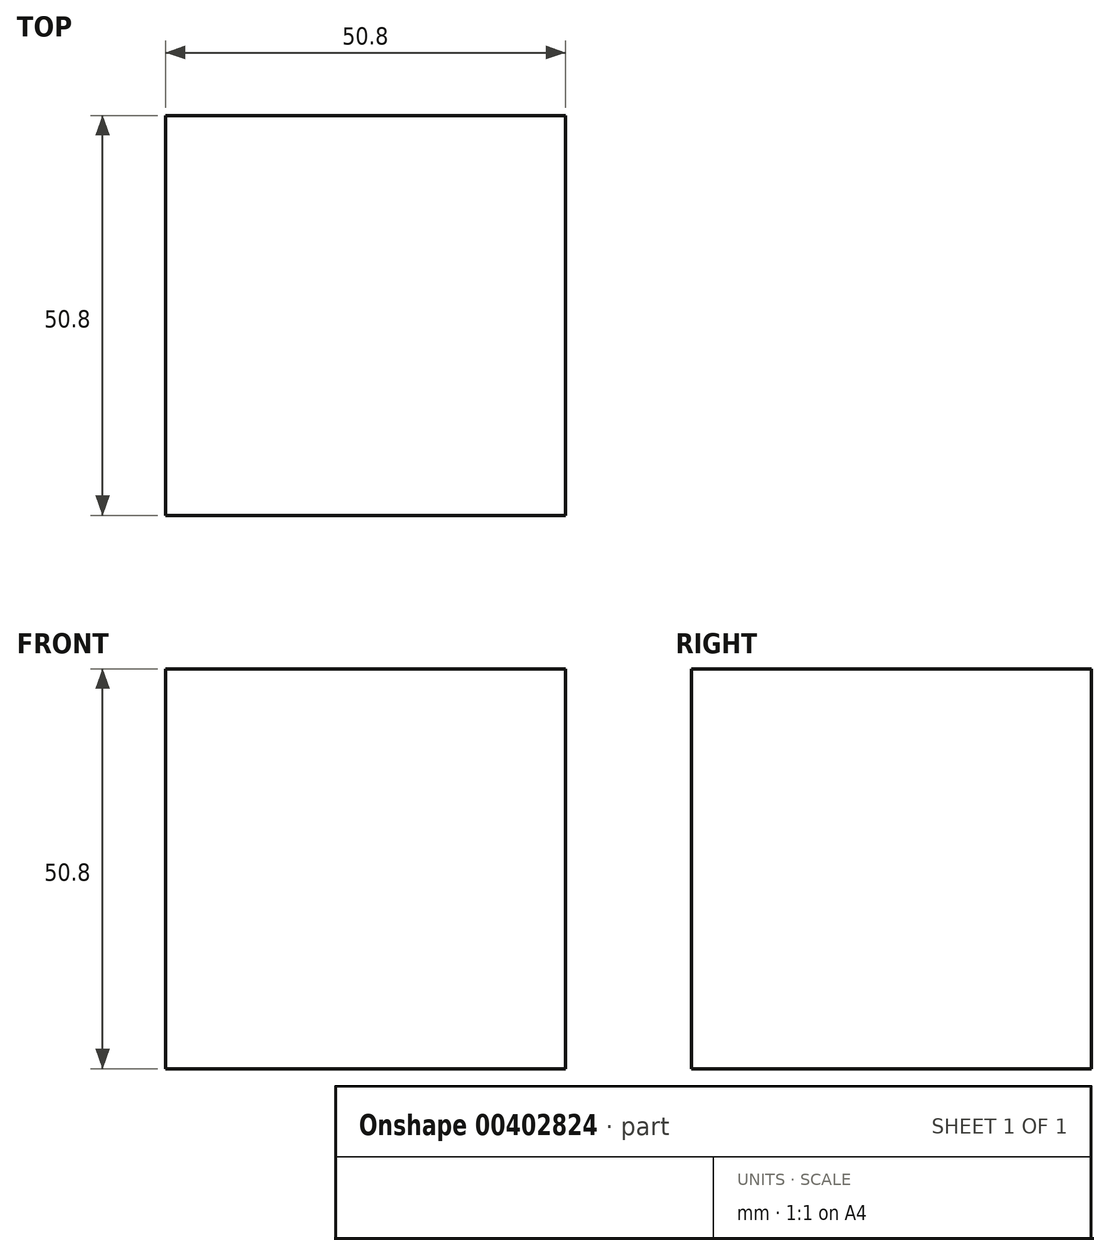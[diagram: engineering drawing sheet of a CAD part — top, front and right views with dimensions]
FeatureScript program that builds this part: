
annotation { "Feature Type Name" : "Feature", "Feature Type Description" : "" }
export const myFeature = defineFeature(function(context is Context, id is Id, definition is map)
    precondition{}
    {
        {
            var Q0;
            Q0=qCreatedBy(makeId("Front.planeOp"),FACE);
            var sketch = newSketch(context, id + "F0", { "sketchPlane" : qUnion([Q0])});
            skLineSegment(sketch, "E0.bottom", {"start": v(0, 0) * mm, "end": v(-50.8, 0) * mm});
            skLineSegment(sketch, "E0.top", {"start": v(0, 50.8) * mm, "end": v(-50.8, 50.8) * mm});
            skLineSegment(sketch, "E0.left", {"start": v(0, 0) * mm, "end": v(0, 50.8) * mm});
            skLineSegment(sketch, "E0.right", {"start": v(-50.8, 0) * mm, "end": v(-50.8, 50.8) * mm});
            skSolve(sketch);
        }
        {
            var Q0;
            Q0=makeQuery(id+"F0.imprint","IMPRINT",FACE,{"disambiguationData":[TD([[makeQuery(id+"F0.imprint","IMPRINT",EDGE,{"derivedFrom":sQuery(id+"F0.wireOp",EDGE,"E0.bottom")}),-1.0]])]});
            extrude(context, id + "F1", {"entities" : qUnion([Q0]), "depth" : 50.8 * mm});
        }
    });
